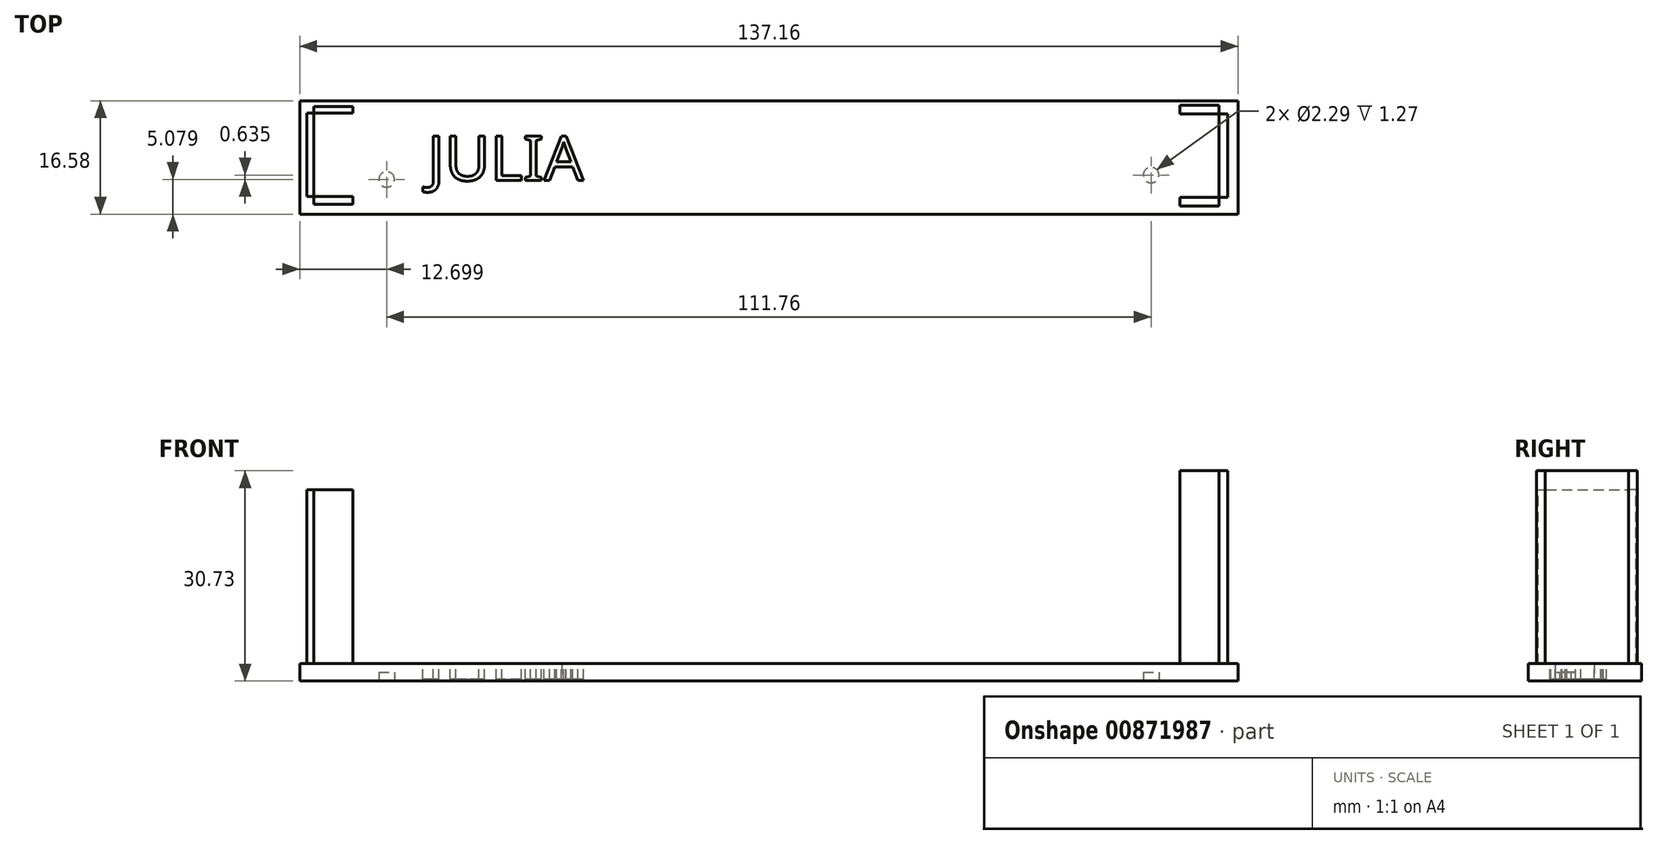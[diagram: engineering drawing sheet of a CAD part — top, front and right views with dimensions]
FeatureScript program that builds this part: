
annotation { "Feature Type Name" : "Feature", "Feature Type Description" : "" }
export const myFeature = defineFeature(function(context is Context, id is Id, definition is map)
    precondition{}
    {
        {
            var Q0;
            Q0=qCreatedBy(makeId("Top.planeOp"),FACE);
            var sketch = newSketch(context, id + "F0", { "sketchPlane" : qUnion([Q0])});
            skLineSegment(sketch, "E0.bottom", {"start": v(-22.02, 19.22) * mm, "end": v(115.14, 19.22) * mm});
            skLineSegment(sketch, "E0.top", {"start": v(-22.02, 5.25) * mm, "end": v(115.14, 5.25) * mm});
            skLineSegment(sketch, "E0.left", {"start": v(-22.02, 19.22) * mm, "end": v(-22.02, 5.25) * mm});
            skLineSegment(sketch, "E0.right", {"start": v(115.14, 19.22) * mm, "end": v(115.14, 5.25) * mm});
            skLineSegment(sketch, "E1", {"start": v(-22.02, 5.25) * mm, "end": v(-19.99, 5.25) * mm});
            skSolve(sketch);
        }
        {
            var Q0;
            Q0=makeQuery(id+"F0.imprint","IMPRINT",FACE,{"disambiguationData":[TD([[makeQuery(id+"F0.imprint","IMPRINT",EDGE,{"derivedFrom":sQuery(id+"F0.wireOp",EDGE,"E0.bottom")}),-1.0]])]});
            extrude(context, id + "F1", {"entities" : qUnion([Q0]), "depth" : 2.54 * mm, "offsetDistance" : 25.4 * mm});
        }
        {
            var Q0;
            Q0=makeQuery(id+"F1.opExtrude","CAP_FACE",FACE,{"disambiguationData":[OSD([sQuery(id+"F0.wireOp",EDGE,"E0.bottom"),sQuery(id+"F0.wireOp",EDGE,"E0.top"),sQuery(id+"F0.wireOp",EDGE,"E0.left"),sQuery(id+"F0.wireOp",EDGE,"E0.right")])],"isStart":false});
            var sketch = newSketch(context, id + "F2", { "sketchPlane" : qUnion([Q0])});
            skLineSegment(sketch, "E2", {"start": v(-22.02, 5.25) * mm, "end": v(-19.99, 5.25) * mm});
            skLineSegment(sketch, "E3", {"start": v(-19.99, 5.25) * mm, "end": v(-19.99, 17.45) * mm});
            skLineSegment(sketch, "E4", {"start": v(-19.99, 17.45) * mm, "end": v(-14.27, 17.45) * mm});
            skLineSegment(sketch, "E5", {"start": v(-19.99, 5.25) * mm, "end": v(-14.27, 5.25) * mm});
            skLineSegment(sketch, "E6", {"start": v(115.14, 5.25) * mm, "end": v(109.42, 5.25) * mm});
            skLineSegment(sketch, "E7", {"start": v(114, 5.25) * mm, "end": v(108.28, 5.25) * mm});
            skSolve(sketch);
        }
        {
            var Q0;
            Q0=sQuery(id+"F2.wireOp",EDGE,"E3");
            var Q1;
            Q1=sQuery(id+"F2.wireOp",EDGE,"E4");
            var Q2;
            Q2=sQuery(id+"F2.wireOp",EDGE,"E5");
            extrude(context, id + "F3", {"bodyType" : ToolBodyType.SURFACE, "surfaceEntities" : qUnion([Q0, Q1, Q2]), "depth" : 25.4 * mm, "offsetDistance" : 25.4 * mm});
        }
        {
            var Q0;
            Q0=makeQuery(id+"F3.opExtrude","SWEPT_FACE",FACE,{"disambiguationData":[OSD([sQuery(id+"F2.wireOp",EDGE,"E3")])]});
            extrude(context, id + "F4", {"entities" : qUnion([Q0]), "operationType" : NewBodyOperationType.ADD, "oppositeDirection" : true, "depth" : 1.02 * mm, "offsetDistance" : 25.4 * mm});
        }
        {
            var Q0;
            Q0=makeQuery(id+"F3.opExtrude","SWEPT_FACE",FACE,{"disambiguationData":[OSD([sQuery(id+"F2.wireOp",EDGE,"E4")])]});
            extrude(context, id + "F5", {"entities" : qUnion([Q0]), "oppositeDirection" : true, "depth" : 0.91 * mm, "offsetDistance" : 25.4 * mm});
        }
        {
            var Q0;
            Q0=makeQuery(id+"F4.boolean.opBoolean","MERGE",FACE,{"derivedFrom":[makeQuery(id+"F1.opExtrude","SWEPT_FACE",FACE,{"disambiguationData":[OSD([sQuery(id+"F0.wireOp",EDGE,"E0.top")])]}),makeQuery(id+"F4.opExtrude","SWEPT_FACE",FACE,{"disambiguationData":[OSD([sQuery(id+"F2.wireOp",VERTEX,"E5.start")])]})]});
            var sketch = newSketch(context, id + "F6", { "sketchPlane" : qUnion([Q0])});
            skLineSegment(sketch, "E8", {"start": v(-21, 2.54) * mm, "end": v(-19.99, 2.54) * mm});
            skSolve(sketch);
        }
        {
            var Q0;
            Q0=makeQuery(id+"F6.imprint","IMPRINT",FACE,{"disambiguationData":[TD([[makeQuery(id+"F6.imprint","IMPRINT",EDGE,{"derivedFrom":sQuery(id+"F6.wireOp",EDGE,"E8")}),-1.0]])]});
            var sketch = newSketch(context, id + "F7", { "sketchPlane" : qUnion([Q0])});
            skLineSegment(sketch, "E9.0", {"start": v(-19.99, 2.54) * mm, "end": v(115.14, 2.54) * mm});
            skLineSegment(sketch, "E10.0", {"start": v(-22.02, 0) * mm, "end": v(115.14, 0) * mm});
            skLineSegment(sketch, "E11.0", {"start": v(-22.02, 2.54) * mm, "end": v(-22.02, 0) * mm});
            skLineSegment(sketch, "E12.0.0", {"start": v(-19.99, 2.54) * mm, "end": v(-21, 2.54) * mm});
            skLineSegment(sketch, "E12.0.1", {"start": v(-21, 2.54) * mm, "end": v(-22.02, 2.54) * mm});
            skLineSegment(sketch, "E12.0.4", {"start": v(115.14, 0) * mm, "end": v(115.14, 2.54) * mm});
            skLineSegment(sketch, "E12.0.5", {"start": v(115.14, 2.54) * mm, "end": v(-19.99, 2.54) * mm});
            skSolve(sketch);
        }
        {
            var Q0;
            Q0=makeQuery(id+"F7.imprint","IMPRINT",FACE,{"disambiguationData":[TD([[makeQuery(id+"F7.imprint","IMPRINT",EDGE,{"derivedFrom":sQuery(id+"F7.wireOp",EDGE,"E12.0.0")}),-1.0]])]});
            extrude(context, id + "F8", {"entities" : qUnion([Q0]), "operationType" : NewBodyOperationType.ADD, "depth" : 2.62 * mm, "offsetDistance" : 25.4 * mm});
        }
        {
            var Q0;
            Q0=makeQuery(id+"F3.opExtrude","SWEPT_FACE",FACE,{"disambiguationData":[OSD([sQuery(id+"F2.wireOp",EDGE,"E5")])]});
            extrude(context, id + "F9", {"entities" : qUnion([Q0]), "oppositeDirection" : true, "depth" : 1.17 * mm, "offsetDistance" : 25.4 * mm});
        }
        {
            var Q0;
            Q0=makeQuery(id+"F8.boolean.opBoolean","MERGE",FACE,{"derivedFrom":[makeQuery(id+"F1.opExtrude","CAP_FACE",FACE,{"disambiguationData":[OSD([sQuery(id+"F0.wireOp",EDGE,"E0.bottom"),sQuery(id+"F0.wireOp",EDGE,"E0.top"),sQuery(id+"F0.wireOp",EDGE,"E0.left"),sQuery(id+"F0.wireOp",EDGE,"E0.right")])],"isStart":false}),makeQuery(id+"F8.opExtrude","SWEPT_FACE",FACE,{"disambiguationData":[OSD([sQuery(id+"F7.wireOp",EDGE,"E12.0.0"),sQuery(id+"F7.wireOp",EDGE,"E12.0.1"),sQuery(id+"F7.wireOp",EDGE,"E12.0.5")])]})]});
            var sketch = newSketch(context, id + "F10", { "sketchPlane" : qUnion([Q0])});
            skLineSegment(sketch, "E13", {"start": v(106.62, 5.12) * mm, "end": v(112.33, 5.12) * mm});
            skLineSegment(sketch, "E14", {"start": v(112.33, 5.12) * mm, "end": v(112.33, 17.32) * mm});
            skLineSegment(sketch, "E15", {"start": v(112.33, 17.32) * mm, "end": v(106.62, 17.32) * mm});
            skSolve(sketch);
        }
        {
            var Q0;
            Q0=sQuery(id+"F10.wireOp",EDGE,"E14");
            var Q1;
            Q1=sQuery(id+"F10.wireOp",EDGE,"E15");
            var Q2;
            Q2=sQuery(id+"F10.wireOp",EDGE,"E13");
            extrude(context, id + "F11", {"bodyType" : ToolBodyType.SURFACE, "surfaceEntities" : qUnion([Q0, Q1, Q2]), "depth" : 28.2 * mm, "offsetDistance" : 25.4 * mm});
        }
        {
            var Q0;
            Q0=makeQuery(id+"F11.opExtrude","SWEPT_FACE",FACE,{"disambiguationData":[OSD([sQuery(id+"F10.wireOp",EDGE,"E15")])]});
            extrude(context, id + "F12", {"entities" : qUnion([Q0]), "operationType" : NewBodyOperationType.ADD, "depth" : 1.27 * mm, "offsetDistance" : 25.4 * mm});
        }
        {
            var Q0;
            Q0=makeQuery(id+"F11.opExtrude","SWEPT_FACE",FACE,{"disambiguationData":[OSD([sQuery(id+"F10.wireOp",EDGE,"E13")])]});
            extrude(context, id + "F13", {"entities" : qUnion([Q0]), "operationType" : NewBodyOperationType.ADD, "depth" : 1.27 * mm, "offsetDistance" : 25.4 * mm});
        }
        {
            var Q0;
            Q0=makeQuery(id+"F11.opExtrude","SWEPT_FACE",FACE,{"disambiguationData":[OSD([sQuery(id+"F10.wireOp",EDGE,"E14")])]});
            extrude(context, id + "F14", {"entities" : qUnion([Q0]), "depth" : 1.27 * mm, "offsetDistance" : 25.4 * mm});
        }
        {
            var Q0;
            Q0=makeQuery(id+"F8.boolean.opBoolean","MERGE",FACE,{"derivedFrom":[makeQuery(id+"F1.opExtrude","CAP_FACE",FACE,{"disambiguationData":[OSD([sQuery(id+"F0.wireOp",EDGE,"E0.bottom"),sQuery(id+"F0.wireOp",EDGE,"E0.top"),sQuery(id+"F0.wireOp",EDGE,"E0.left"),sQuery(id+"F0.wireOp",EDGE,"E0.right")])],"isStart":true}),makeQuery(id+"F8.opExtrude","SWEPT_FACE",FACE,{"disambiguationData":[OSD([sQuery(id+"F7.wireOp",EDGE,"E10.0")])]})]});
            var sketch = newSketch(context, id + "F15", { "sketchPlane" : qUnion([Q0])});
            skLineSegment(sketch, "E16", {"start": v(-22.02, -2.64) * mm, "end": v(-9.32, -2.64) * mm});
            skLineSegment(sketch, "E17", {"start": v(-9.32, -2.64) * mm, "end": v(-9.32, -7.72) * mm});
            skCircle(sketch, "E18", {"center": v(-9.32, -7.72) * mm, "radius": 2.86 * mm});
            skCircle(sketch, "E19", {"center": v(-9.32, -7.72) * mm, "radius": 1.14 * mm});
            skLineSegment(sketch, "E20", {"start": v(115.14, -2.64) * mm, "end": v(102.44, -2.64) * mm});
            skLineSegment(sketch, "E21", {"start": v(102.44, -2.64) * mm, "end": v(102.44, -8.35) * mm});
            skCircle(sketch, "E22", {"center": v(102.44, -8.35) * mm, "radius": 1.14 * mm});
            skSolve(sketch);
        }
        {
            var Q0;
            Q0=makeQuery(id+"F15.imprint","IMPRINT",FACE,{"disambiguationData":[TD([[makeQuery(id+"F15.imprint","IMPRINT",EDGE,{"derivedFrom":sQuery(id+"F15.wireOp",EDGE,"E19")}),1.0]])]});
            extrude(context, id + "F16", {"entities" : qUnion([Q0]), "operationType" : NewBodyOperationType.REMOVE, "oppositeDirection" : true, "depth" : 1.27 * mm, "offsetDistance" : 25.4 * mm});
        }
        {
            var Q0;
            Q0=makeQuery(id+"F15.imprint","IMPRINT",FACE,{"disambiguationData":[TD([[makeQuery(id+"F15.imprint","IMPRINT",EDGE,{"derivedFrom":sQuery(id+"F15.wireOp",EDGE,"E22")}),1.0]])]});
            extrude(context, id + "F17", {"entities" : qUnion([Q0]), "operationType" : NewBodyOperationType.REMOVE, "oppositeDirection" : true, "depth" : 1.27 * mm, "offsetDistance" : 25.4 * mm});
        }
        {
            var Q0;
            Q0=makeQuery(id+"F8.boolean.opBoolean","MERGE",FACE,{"derivedFrom":[makeQuery(id+"F1.opExtrude","CAP_FACE",FACE,{"disambiguationData":[OSD([sQuery(id+"F0.wireOp",EDGE,"E0.bottom"),sQuery(id+"F0.wireOp",EDGE,"E0.top"),sQuery(id+"F0.wireOp",EDGE,"E0.left"),sQuery(id+"F0.wireOp",EDGE,"E0.right")])],"isStart":false}),makeQuery(id+"F8.opExtrude","SWEPT_FACE",FACE,{"disambiguationData":[OSD([sQuery(id+"F7.wireOp",EDGE,"E12.0.0"),sQuery(id+"F7.wireOp",EDGE,"E12.0.1"),sQuery(id+"F7.wireOp",EDGE,"E12.0.5")])]})]});
            var sketch = newSketch(context, id + "F18", { "sketchPlane" : qUnion([Q0])});
            skText(sketch, "E23", { "text": "JULIA", "fontName": "NotoSans-Regular.ttf"});
            const initialGuessF18  = {"E23": [-0.00332, 0.00756, 1, 0, 0.00655]};
            skSetInitialGuess(sketch, initialGuessF18);
            skSolve(sketch);
        }
        {
            var Q0;
            Q0 = qSketchRegion(id + "F18", true);
            extrude(context, id + "F19", {"entities" : qUnion([Q0]), "operationType" : NewBodyOperationType.REMOVE, "oppositeDirection" : true, "depth" : 2.3 * mm, "offsetDistance" : 25.4 * mm});
        }
    });
